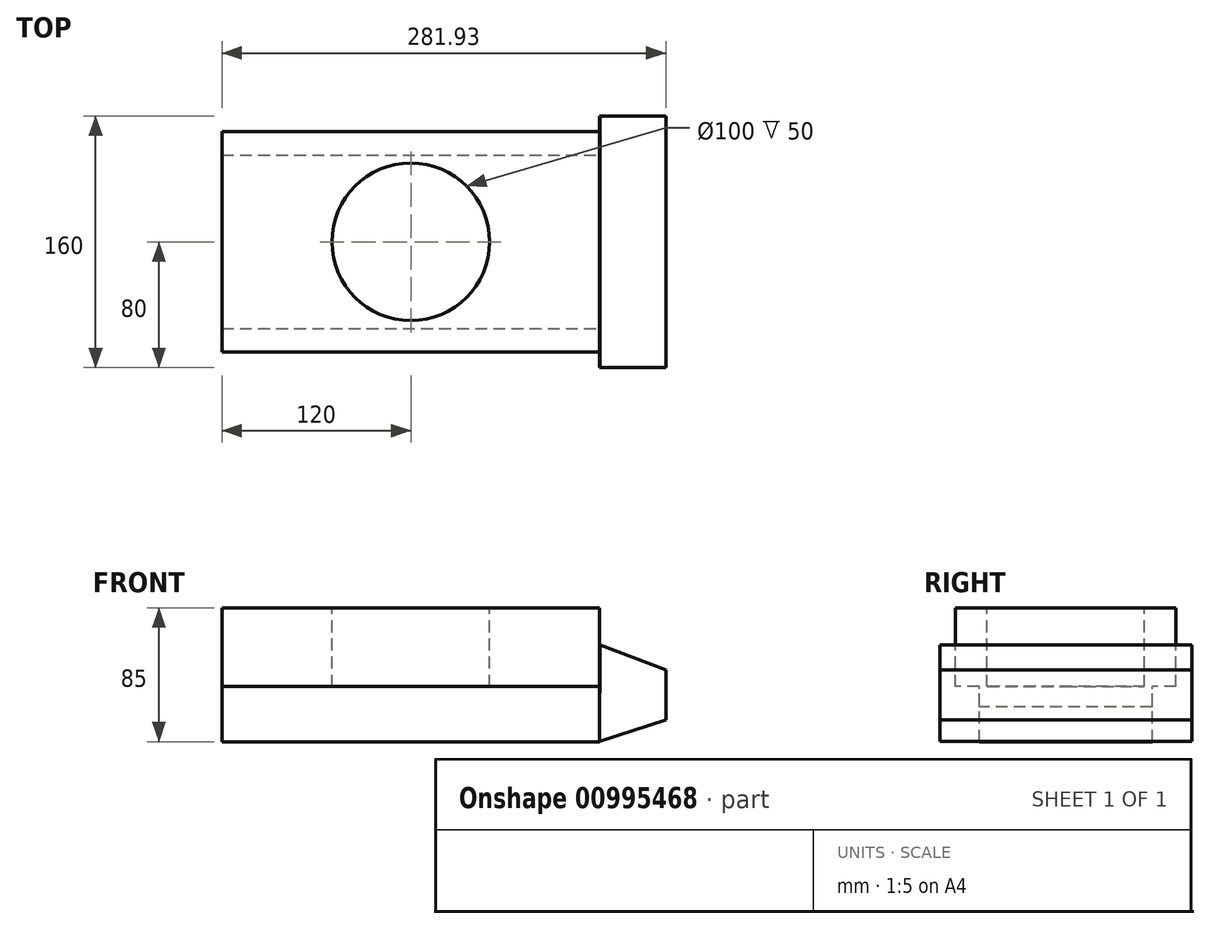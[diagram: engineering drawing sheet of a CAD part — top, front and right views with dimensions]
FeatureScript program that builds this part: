
annotation { "Feature Type Name" : "Feature", "Feature Type Description" : "" }
export const myFeature = defineFeature(function(context is Context, id is Id, definition is map)
    precondition{}
    {
        {
            var Q0;
            Q0=qCreatedBy(makeId("Top.planeOp"),FACE);
            var sketch = newSketch(context, id + "F0", { "sketchPlane" : qUnion([Q0])});
            skCircle(sketch, "E0", {"center": v(0, 0) * mm, "radius": 50 * mm});
            skLineSegment(sketch, "E1.bottom", {"start": v(-120, 70) * mm, "end": v(120, 70) * mm});
            skLineSegment(sketch, "E1.top", {"start": v(-120, -70) * mm, "end": v(120, -70) * mm});
            skLineSegment(sketch, "E1.left", {"start": v(-120, 70) * mm, "end": v(-120, -70) * mm});
            skLineSegment(sketch, "E1.right", {"start": v(120, 70) * mm, "end": v(120, -70) * mm});
            skLineSegment(sketch, "E2", {"start": v(0, 0) * mm, "end": v(0, 70) * mm});
            skSolve(sketch);
        }
        {
            var Q0;
            Q0=makeQuery(id+"F0.imprint","IMPRINT",FACE,{"disambiguationData":[TD([[makeQuery(id+"F0.imprint","IMPRINT",EDGE,{"derivedFrom":sQuery(id+"F0.wireOp",EDGE,"E0")}),-1.0]])]});
            extrude(context, id + "F1", {"entities" : qUnion([Q0]), "oppositeDirection" : true, "depth" : 50 * mm, "offsetDistance" : 25 * mm});
        }
        {
            var Q0;
            Q0=makeQuery(id+"F1.opExtrude","CAP_FACE",FACE,{"disambiguationData":[OSD([sQuery(id+"F0.wireOp",EDGE,"E0"),sQuery(id+"F0.wireOp",EDGE,"E1.bottom"),sQuery(id+"F0.wireOp",EDGE,"E1.top"),sQuery(id+"F0.wireOp",EDGE,"E1.left"),sQuery(id+"F0.wireOp",EDGE,"E1.right")])],"isStart":false});
            var sketch = newSketch(context, id + "F2", { "sketchPlane" : qUnion([Q0])});
            skLineSegment(sketch, "E3.bottom", {"start": v(-120, 55) * mm, "end": v(120, 55) * mm});
            skLineSegment(sketch, "E3.top", {"start": v(-120, -55) * mm, "end": v(120, -55) * mm});
            skLineSegment(sketch, "E3.left", {"start": v(-120, 55) * mm, "end": v(-120, -55) * mm});
            skLineSegment(sketch, "E3.right", {"start": v(120, 55) * mm, "end": v(120, -55) * mm});
            skPoint(sketch, "E3.middle", {"position": v(0, 0) * mm});
            skSolve(sketch);
        }
        {
            var Q0;
            Q0=makeQuery(id+"F2.imprint","IMPRINT",FACE,{"disambiguationData":[TD([[makeQuery(id+"F2.imprint","IMPRINT",EDGE,{"derivedFrom":sQuery(id+"F2.wireOp",EDGE,"E3.bottom")}),-1.0]])]});
            var Q1;
            Q1=makeQuery(id+"F2.imprint","IMPRINT",FACE,{"disambiguationData":[TD([[makeQuery(id+"F2.imprint","IMPRINT",EDGE,{"derivedFrom":makeQuery(id+"F1.opExtrude","CAP_EDGE",EDGE,{"disambiguationData":[OSD([sQuery(id+"F0.wireOp",EDGE,"E0")])],"isStart":false})}),-1.0]])]});
            extrude(context, id + "F3", {"entities" : qUnion([Q0, Q1]), "operationType" : NewBodyOperationType.ADD, "depth" : 35 * mm, "offsetDistance" : 25 * mm});
        }
        {
            var Q0;
            Q0=qCreatedBy(makeId("Front.planeOp"),FACE);
            var sketch = newSketch(context, id + "F4", { "sketchPlane" : qUnion([Q0])});
            skLineSegment(sketch, "E4", {"start": v(120.13, -23.61) * mm, "end": v(161.93, -39.34) * mm});
            skLineSegment(sketch, "E5", {"start": v(161.93, -39.34) * mm, "end": v(161.93, -71.18) * mm});
            skLineSegment(sketch, "E6", {"start": v(161.93, -71.18) * mm, "end": v(119.93, -84.92) * mm});
            skLineSegment(sketch, "E7", {"start": v(120.13, -23.61) * mm, "end": v(119.93, -84.92) * mm});
            skSolve(sketch);
        }
        {
            var Q0;
            Q0 = qSketchRegion(id + "F4", true);
            extrude(context, id + "F5", {"entities" : qUnion([Q0]), "operationType" : NewBodyOperationType.ADD, "endBound" : BoundingType.SYMMETRIC, "depth" : 160 * mm, "offsetDistance" : 25 * mm});
        }
    });
